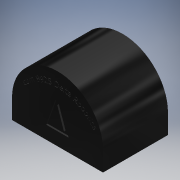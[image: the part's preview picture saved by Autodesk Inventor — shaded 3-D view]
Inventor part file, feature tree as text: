
AUTODESK INVENTOR PART (.ipt)
format: ipt  version: 2019 (Build 230136000, 136)  size: 700,416 bytes
history: native  units: mm (DEFAULTED — no unit token found)
features: extrude x5, sketch x5, shell x1, projected_geometry x1
ambient origin geometry x8: Origin, YZ Plane, XZ Plane, XY Plane, X Axis, Y Axis, Z Axis, Center Point
bodies: Body1 (feature_tree)
feature tree (12):
  extrude  "Extrusion2"  Depth=63.5mm TaperAngle=0.0deg
  shell  "Shell2"  Thickness=3.175mm
  extrude  "Extrusion3"  Depth=19.05mm TaperAngle=0.0deg
  extrude  "Extrusion6"  Depth=25.4mm
  extrude  "Extrusion10"  Depth=38.1mm
  extrude  "Extrusion12"  TaperAngle=0.0deg  [1 undecoded]
  sketch  "Sketch2"  dims[d3=88.9mm d7=63.5mm d8=0.0mm d9=3.175mm]
  sketch  "Sketch3"  dims[d10=3.175mm d11=0.0mm d19=19.05mm d20=0.0mm]
  sketch  "Sketch8"  dims[d55=25.4mm d56=25.4mm]
  projected_geometry  "Projected Loop2"
  sketch  "Sketch15"  dims[d57=12.7mm d58=38.1mm]
  sketch  "Sketch16"  dims[d59=1.5875mm d60=0.0mm d64=0.0mm d65=1.5875mm d66=0.0mm]
note: 1 required parameter value undecoded (feature->parameter linkage not recoverable at this tier; creation-order binding heuristic only, values carry confidence <= 0.55)
